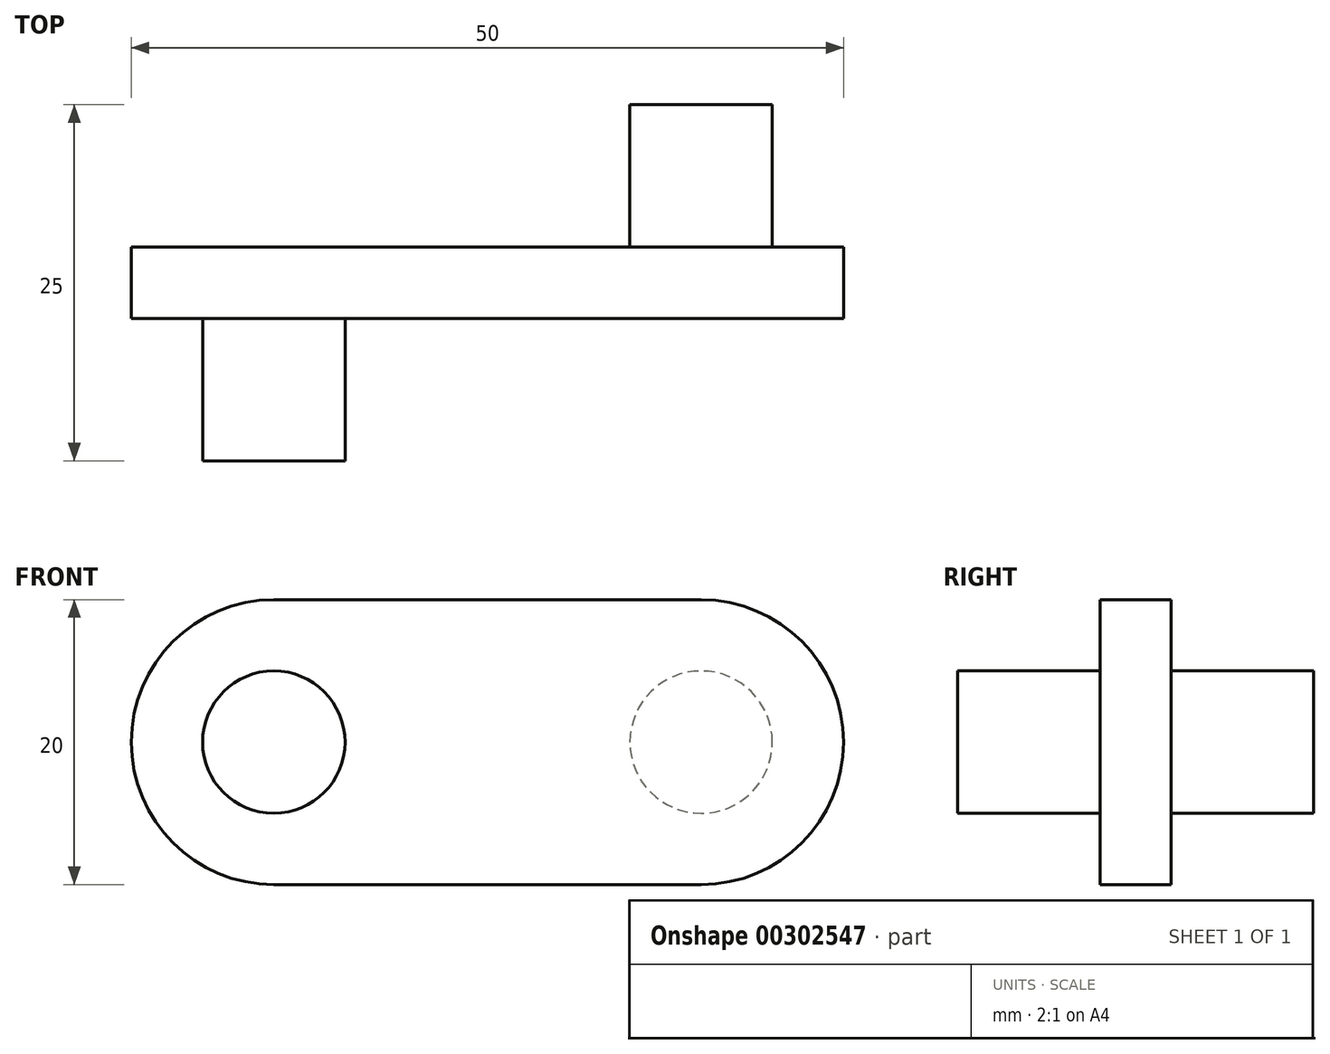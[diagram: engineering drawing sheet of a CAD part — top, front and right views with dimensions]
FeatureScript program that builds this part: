
annotation { "Feature Type Name" : "Feature", "Feature Type Description" : "" }
export const myFeature = defineFeature(function(context is Context, id is Id, definition is map)
    precondition{}
    {
        {
            var Q0;
            Q0=qCreatedBy(makeId("Front.planeOp"),FACE);
            var sketch = newSketch(context, id + "F0", { "sketchPlane" : qUnion([Q0])});
            skLineSegment(sketch, "E0", {"start": v(0, 10) * mm, "end": v(30, 10) * mm});
            skLineSegment(sketch, "E1", {"start": v(30, -10) * mm, "end": v(0, -10) * mm});
            skCircle(sketch, "E2", {"center": v(30, 0) * mm, "radius": 5 * mm});
            skCircle(sketch, "E3", {"center": v(0, 0) * mm, "radius": 5 * mm});
            skArc(sketch, "E4", {"start": v(30, -10) * mm, "mid": v(40, 0) * mm, "end": v(30, 10) * mm});
            skArc(sketch, "E5", {"start": v(0, 10) * mm, "mid": v(-10, 0) * mm, "end": v(0, -10) * mm});
            skSolve(sketch);
        }
        {
            var Q0;
            Q0=makeQuery(id+"F0.imprint","IMPRINT",FACE,{"disambiguationData":[TD([[makeQuery(id+"F0.imprint","IMPRINT",EDGE,{"derivedFrom":sQuery(id+"F0.wireOp",EDGE,"E0")}),-1.0]])]});
            extrude(context, id + "F1", {"entities" : qUnion([Q0]), "depth" : 5 * mm});
        }
        {
            var Q0;
            Q0=makeQuery(id+"F0.imprint","IMPRINT",FACE,{"disambiguationData":[TD([[makeQuery(id+"F0.imprint","IMPRINT",EDGE,{"derivedFrom":sQuery(id+"F0.wireOp",EDGE,"E3")}),1.0]])]});
            extrude(context, id + "F2", {"entities" : qUnion([Q0]), "operationType" : NewBodyOperationType.ADD, "depth" : 15 * mm});
        }
        {
            var Q0;
            Q0=makeQuery(id+"F0.imprint","IMPRINT",FACE,{"disambiguationData":[TD([[makeQuery(id+"F0.imprint","IMPRINT",EDGE,{"derivedFrom":sQuery(id+"F0.wireOp",EDGE,"E2")}),1.0]])]});
            extrude(context, id + "F3", {"entities" : qUnion([Q0]), "operationType" : NewBodyOperationType.ADD, "oppositeDirection" : true, "depth" : 10 * mm, "hasSecondDirection" : true, "secondDirectionOppositeDirection" : false, "secondDirectionDepth" : 5 * mm});
        }
    });
